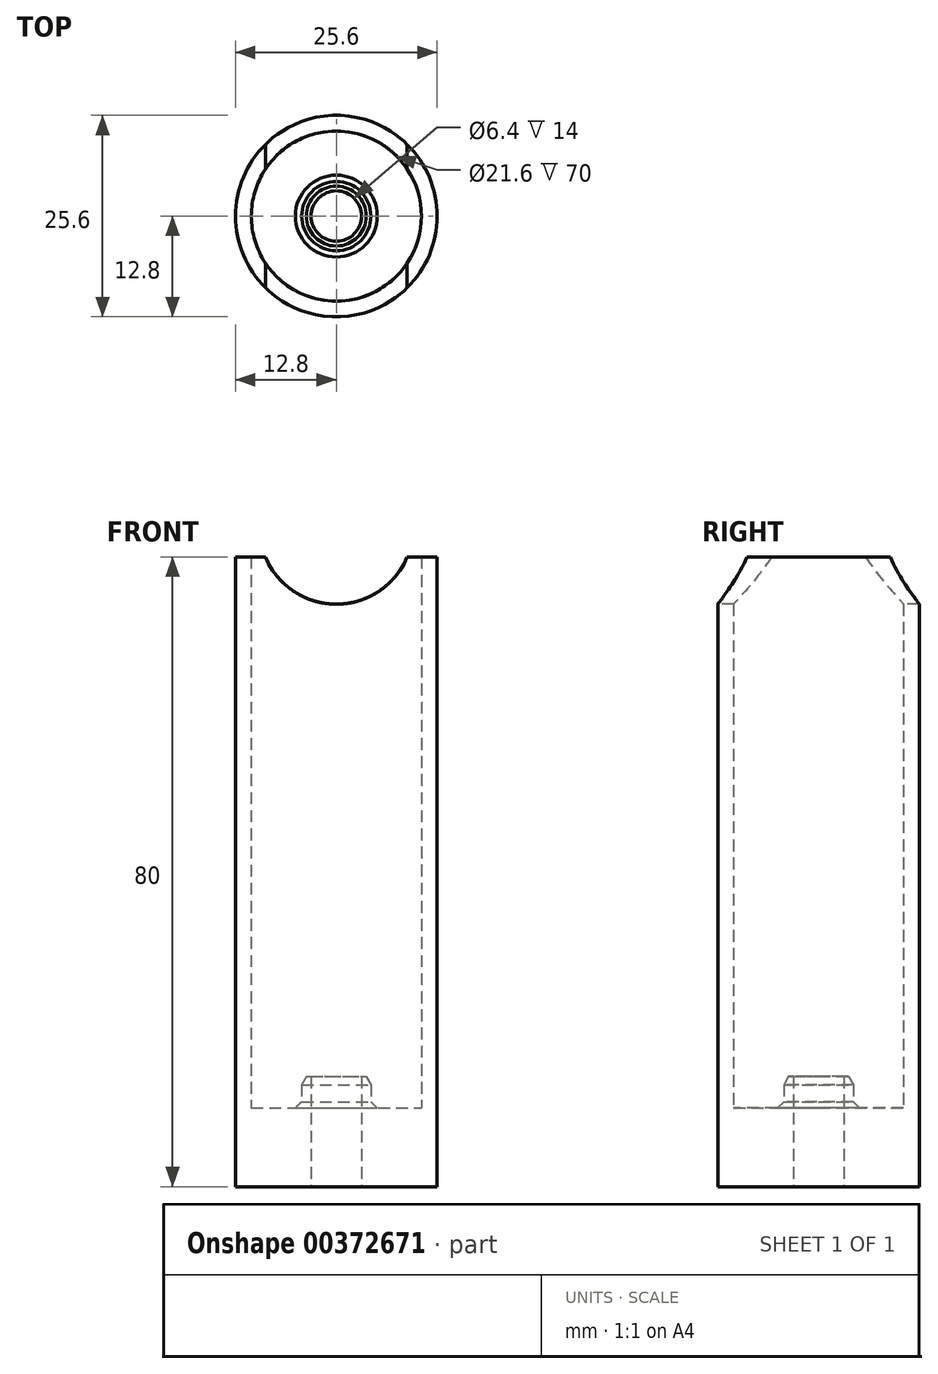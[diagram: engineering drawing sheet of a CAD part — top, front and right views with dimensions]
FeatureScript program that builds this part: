
annotation { "Feature Type Name" : "Feature", "Feature Type Description" : "" }
export const myFeature = defineFeature(function(context is Context, id is Id, definition is map)
    precondition{}
    {
        {
            var Q0;
            Q0=qCreatedBy(makeId("Front.planeOp"),FACE);
            var sketch = newSketch(context, id + "F0", { "sketchPlane" : qUnion([Q0])});
            skLineSegment(sketch, "E0", {"start": v(12.8, 0) * mm, "end": v(12.8, 80) * mm});
            skLineSegment(sketch, "E1", {"start": v(12.8, 80) * mm, "end": v(10.8, 80) * mm});
            skLineSegment(sketch, "E2", {"start": v(10.8, 80) * mm, "end": v(10.8, 10) * mm});
            skLineSegment(sketch, "E3", {"start": v(10.8, 10) * mm, "end": v(5.2, 10) * mm});
            skLineSegment(sketch, "E4", {"start": v(4.4, 12.96) * mm, "end": v(3.8, 14) * mm});
            skLineSegment(sketch, "E5", {"start": v(3.8, 14) * mm, "end": v(3.2, 14) * mm});
            skLineSegment(sketch, "E6", {"start": v(3.2, 14) * mm, "end": v(3.2, 0) * mm});
            skLineSegment(sketch, "E7", {"start": v(3.2, 0) * mm, "end": v(12.8, 0) * mm});
            skLineSegment(sketch, "E8", {"start": v(4.4, 10.8) * mm, "end": v(4.4, 12.96) * mm});
            skLineSegment(sketch, "E9", {"start": v(4.4, 10.8) * mm, "end": v(5.2, 10) * mm});
            skPoint(sketch, "E10.orphan", {"position": v(4.4, 10) * mm});
            skLineSegment(sketch, "E11", {"start": v(0, 0) * mm, "end": v(0, 74.05) * mm, "construction": true});
            skSolve(sketch);
        }
        {
            var Q0;
            Q0=makeQuery(id+"F0.imprint","IMPRINT",FACE,{"disambiguationData":[TD([[makeQuery(id+"F0.imprint","IMPRINT",EDGE,{"derivedFrom":sQuery(id+"F0.wireOp",EDGE,"E0")}),1.0]])]});
            var Q1;
            Q1=sQuery(id+"F0.wireOp",EDGE,"E11");
            revolve(context, id + "F1", {"surfaceOperationType" : NewSurfaceOperationType.NEW, "entities" : qUnion([Q0]), "axis" : qUnion([Q1]), "revolveType" : RevolveType.FULL});
        }
        {
            var Q0;
            Q0=qCreatedBy(makeId("Front.planeOp"),FACE);
            var sketch = newSketch(context, id + "F2", { "sketchPlane" : qUnion([Q0])});
            skArc(sketch, "E12", {"start": v(-9, 80) * mm, "mid": v(0, 74) * mm, "end": v(9, 80) * mm});
            skLineSegment(sketch, "E13", {"start": v(-9, 80) * mm, "end": v(9, 80) * mm});
            skSolve(sketch);
        }
        {
            var Q0;
            Q0 = qSketchRegion(id + "F2", true);
            extrude(context, id + "F3", {"entities" : qUnion([Q0]), "operationType" : NewBodyOperationType.REMOVE, "endBound" : BoundingType.THROUGH_ALL, "oppositeDirection" : true, "depth" : 25 * mm, "offsetDistance" : 25 * mm, "hasSecondDirection" : true, "secondDirectionBound" : BoundingType.THROUGH_ALL, "secondDirectionOppositeDirection" : false, "secondDirectionDepth" : 25 * mm});
        }
    });
